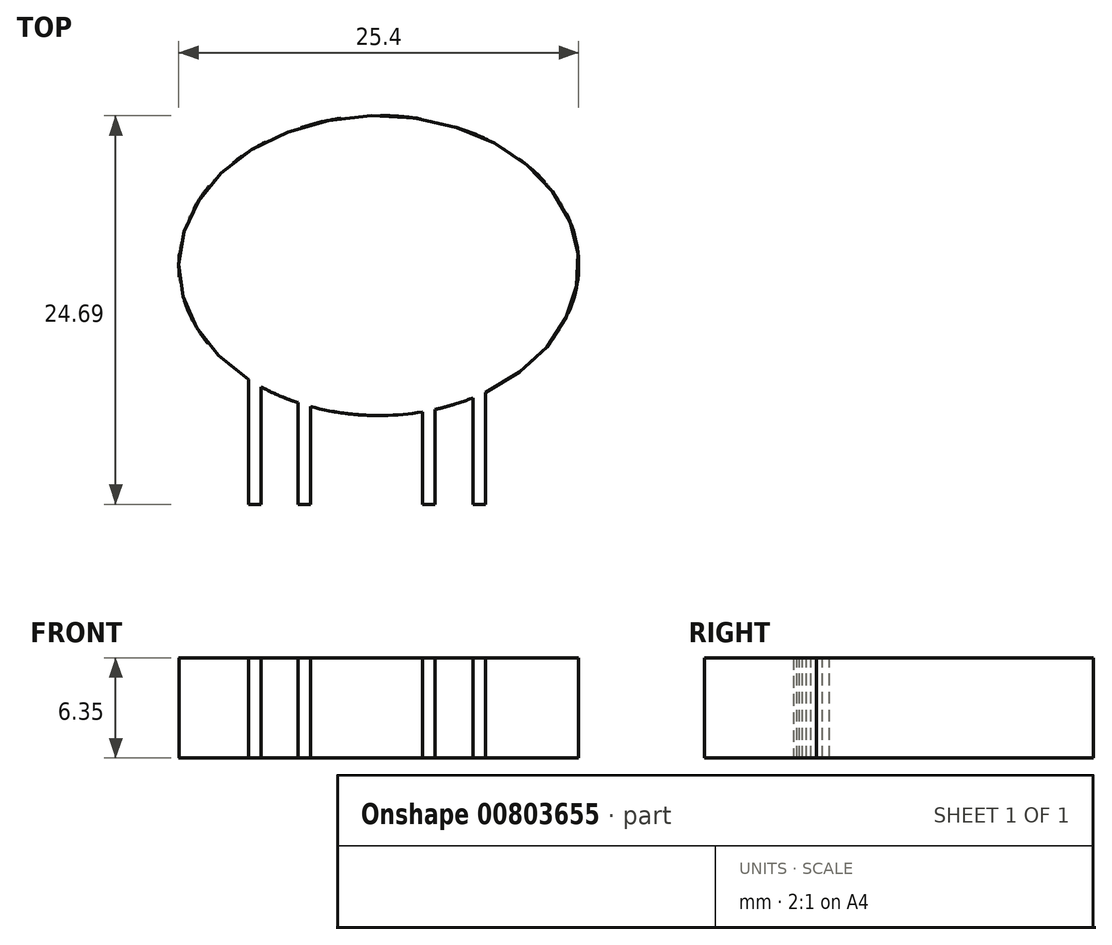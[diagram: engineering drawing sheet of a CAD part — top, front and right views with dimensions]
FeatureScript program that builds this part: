
annotation { "Feature Type Name" : "Feature", "Feature Type Description" : "" }
export const myFeature = defineFeature(function(context is Context, id is Id, definition is map)
    precondition{}
    {
        {
            var Q0;
            Q0=qCreatedBy(makeId("Top.planeOp"),FACE);
            var sketch = newSketch(context, id + "F0", { "sketchPlane" : qUnion([Q0])});
            skEllipse(sketch, "E0", {"center": v(0, 0) * mm, "majorRadius": 12.7 * mm, "minorRadius": 9.53 * mm, "majorAxis": v(1, 0)});
            skSolve(sketch);
        }
        {
            var Q0;
            Q0=makeQuery(id+"F0.imprint","IMPRINT",FACE,{"disambiguationData":[TD([[makeQuery(id+"F0.imprint","IMPRINT",EDGE,{"derivedFrom":sQuery(id+"F0.wireOp",EDGE,"4oxSIaH4-2MgM-J6ta-eGWN-qDmhUPtUYjd6")}),1.0]])]});
            var Q1;
            Q1=makeQuery(id+"F0.imprint","IMPRINT",FACE,{"disambiguationData":[TD([[makeQuery(id+"F0.imprint","IMPRINT",EDGE,{"derivedFrom":sQuery(id+"F0.wireOp",EDGE,"E0")}),1.0]])]});
            extrude(context, id + "F1", {"entities" : qUnion([Q0, Q1]), "depth" : 6.35 * mm, "offsetDistance" : 25.4 * mm});
        }
        {
            var Q0;
            Q0=makeQuery(id+"F1.opExtrude","CAP_FACE",FACE,{"disambiguationData":[OSD([sQuery(id+"F0.wireOp",EDGE,"E0")])],"isStart":false});
            var sketch = newSketch(context, id + "F2", { "sketchPlane" : qUnion([Q0])});
            skLineSegment(sketch, "E1", {"start": v(-12.7, 0) * mm, "end": v(-7.92, 0) * mm, "construction": true});
            skLineSegment(sketch, "E2", {"start": v(-7.92, 0) * mm, "end": v(-4.75, 0) * mm, "construction": true});
            skLineSegment(sketch, "E3", {"start": v(-4.75, 0) * mm, "end": v(3.18, 0) * mm, "construction": true});
            skLineSegment(sketch, "E4", {"start": v(3.18, 0) * mm, "end": v(6.35, 0) * mm, "construction": true});
            skLineSegment(sketch, "E5", {"start": v(6.35, 0) * mm, "end": v(12.7, 0) * mm, "construction": true});
            skLineSegment(sketch, "E6", {"start": v(-7.92, 0) * mm, "end": v(-7.92, -7.44) * mm, "construction": true});
            skLineSegment(sketch, "E7", {"start": v(-4.75, 0) * mm, "end": v(-4.75, -8.83) * mm, "construction": true});
            skLineSegment(sketch, "E8", {"start": v(3.18, 0) * mm, "end": v(3.18, -9.22) * mm, "construction": true});
            skLineSegment(sketch, "E9", {"start": v(6.35, 0) * mm, "end": v(6.35, -8.25) * mm, "construction": true});
            skLineSegment(sketch, "E10", {"start": v(-7.92, -7.44) * mm, "end": v(-8.26, -7.23) * mm});
            skLineSegment(sketch, "E11", {"start": v(-8.26, -7.23) * mm, "end": v(-8.26, -15.17) * mm});
            skLineSegment(sketch, "E12", {"start": v(-8.26, -15.17) * mm, "end": v(-7.47, -15.17) * mm});
            skLineSegment(sketch, "E13", {"start": v(-7.47, -15.17) * mm, "end": v(-7.47, -7.7) * mm});
            skLineSegment(sketch, "E14", {"start": v(-7.47, -7.7) * mm, "end": v(-7.92, -7.44) * mm});
            skLineSegment(sketch, "E15", {"start": v(-4.75, -8.83) * mm, "end": v(-5.14, -8.71) * mm});
            skLineSegment(sketch, "E16", {"start": v(-5.14, -8.71) * mm, "end": v(-5.14, -15.17) * mm});
            skLineSegment(sketch, "E17", {"start": v(-5.14, -15.17) * mm, "end": v(-4.34, -15.17) * mm});
            skLineSegment(sketch, "E18", {"start": v(-4.34, -15.17) * mm, "end": v(-4.34, -8.95) * mm});
            skLineSegment(sketch, "E19", {"start": v(-4.34, -8.95) * mm, "end": v(-4.75, -8.83) * mm});
            skLineSegment(sketch, "E20", {"start": v(3.18, -9.22) * mm, "end": v(2.78, -9.3) * mm});
            skLineSegment(sketch, "E21", {"start": v(2.78, -9.3) * mm, "end": v(2.78, -15.17) * mm});
            skLineSegment(sketch, "E22", {"start": v(2.78, -15.17) * mm, "end": v(3.57, -15.17) * mm});
            skLineSegment(sketch, "E23", {"start": v(3.57, -15.17) * mm, "end": v(3.57, -9.14) * mm});
            skLineSegment(sketch, "E24", {"start": v(3.57, -9.14) * mm, "end": v(3.18, -9.22) * mm});
            skLineSegment(sketch, "E25", {"start": v(6.35, -8.25) * mm, "end": v(5.97, -8.4) * mm});
            skLineSegment(sketch, "E26", {"start": v(5.97, -8.4) * mm, "end": v(5.97, -15.17) * mm});
            skLineSegment(sketch, "E27", {"start": v(5.97, -15.17) * mm, "end": v(6.77, -15.17) * mm});
            skLineSegment(sketch, "E28", {"start": v(6.77, -15.17) * mm, "end": v(6.77, -8.06) * mm});
            skLineSegment(sketch, "E29", {"start": v(6.77, -8.06) * mm, "end": v(6.35, -8.25) * mm});
            skSolve(sketch);
        }
        {
            var Q0;
            Q0 = qSketchRegion(id + "F2", true);
            extrude(context, id + "F3", {"entities" : qUnion([Q0]), "operationType" : NewBodyOperationType.ADD, "oppositeDirection" : true, "depth" : 6.35 * mm, "offsetDistance" : 25.4 * mm});
        }
    });
